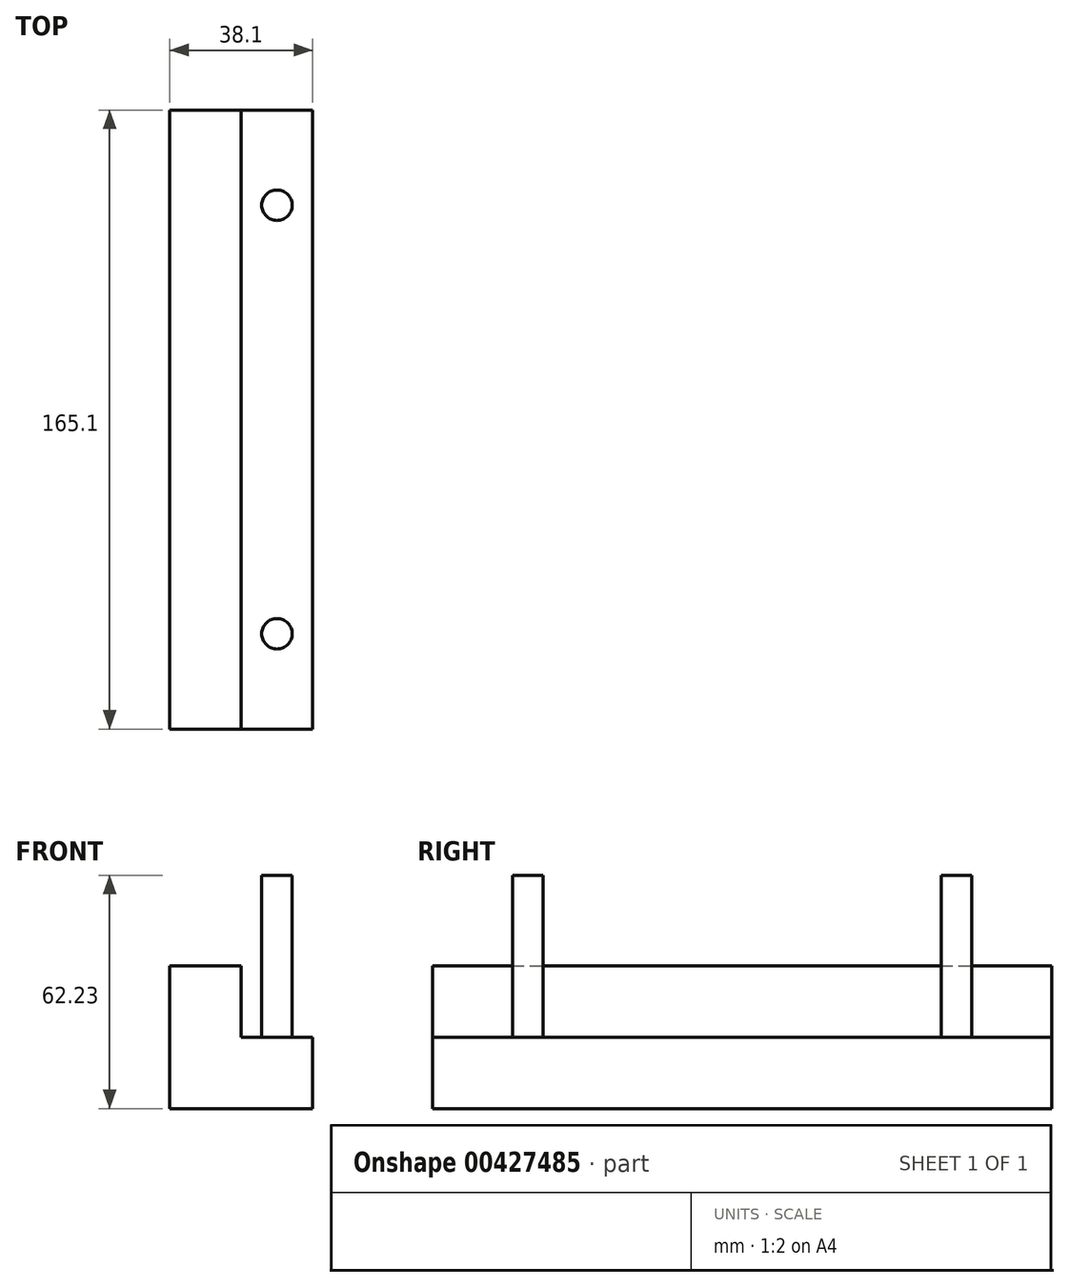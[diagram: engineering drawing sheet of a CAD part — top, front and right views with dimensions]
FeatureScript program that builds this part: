
annotation { "Feature Type Name" : "Feature", "Feature Type Description" : "" }
export const myFeature = defineFeature(function(context is Context, id is Id, definition is map)
    precondition{}
    {
        {
            var Q0;
            Q0=qCreatedBy(makeId("Front.planeOp"),FACE);
            var sketch = newSketch(context, id + "F0", { "sketchPlane" : qUnion([Q0])});
            skLineSegment(sketch, "E0.bottom", {"start": v(0, 0) * mm, "end": v(38.1, 0) * mm});
            skLineSegment(sketch, "E0.top", {"start": v(0, 38.1) * mm, "end": v(19.05, 38.1) * mm});
            skLineSegment(sketch, "E0.left", {"start": v(0, 0) * mm, "end": v(0, 38.1) * mm});
            skLineSegment(sketch, "E0.right", {"start": v(38.1, 0) * mm, "end": v(38.1, 19.05) * mm});
            skLineSegment(sketch, "E1.top", {"start": v(38.1, 19.05) * mm, "end": v(19.05, 19.05) * mm});
            skLineSegment(sketch, "E1.right", {"start": v(19.05, 38.1) * mm, "end": v(19.05, 19.05) * mm});
            skSolve(sketch);
        }
        {
            var Q0;
            Q0 = qSketchRegion(id + "F0", true);
            extrude(context, id + "F1", {"entities" : qUnion([Q0]), "depth" : 165.1 * mm});
        }
        {
            var Q0;
            Q0=makeQuery(id+"F1.opExtrude","SWEPT_FACE",FACE,{"disambiguationData":[OSD([sQuery(id+"F0.wireOp",EDGE,"E1.top")])]});
            var sketch = newSketch(context, id + "F2", { "sketchPlane" : qUnion([Q0])});
            skCircle(sketch, "E2", {"center": v(28.58, -25.4) * mm, "radius": 4.06 * mm});
            skCircle(sketch, "E3", {"center": v(28.58, -139.7) * mm, "radius": 4.06 * mm});
            skSolve(sketch);
        }
        {
            var Q0;
            Q0 = qSketchRegion(id + "F2", true);
            extrude(context, id + "F3", {"entities" : qUnion([Q0]), "operationType" : NewBodyOperationType.ADD, "depth" : 43.18 * mm});
        }
    });
